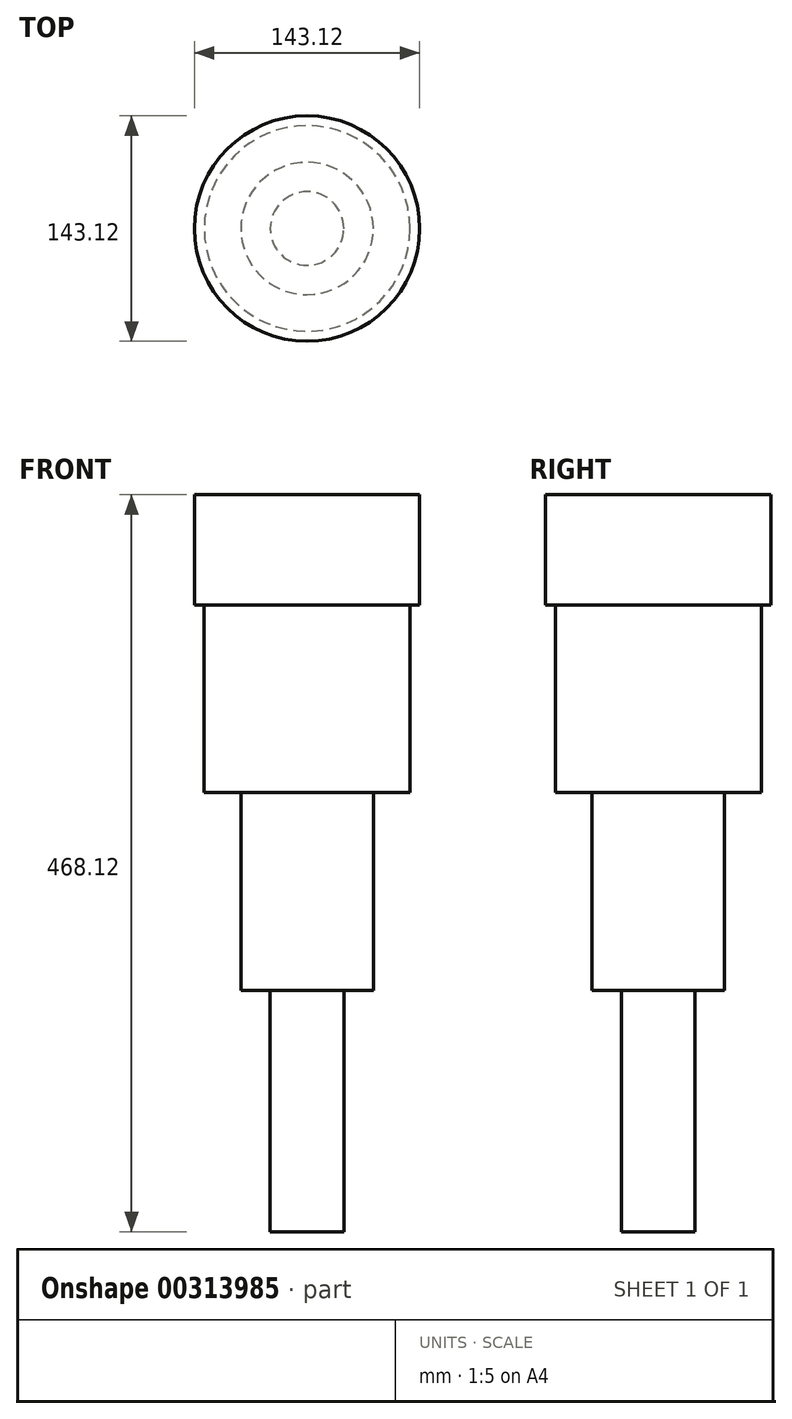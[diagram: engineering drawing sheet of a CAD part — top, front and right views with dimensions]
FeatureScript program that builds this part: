
annotation { "Feature Type Name" : "Feature", "Feature Type Description" : "" }
export const myFeature = defineFeature(function(context is Context, id is Id, definition is map)
    precondition{}
    {
        {
            var Q0;
            Q0=qCreatedBy(makeId("Top.planeOp"),FACE);
            var sketch = newSketch(context, id + "F0", { "sketchPlane" : qUnion([Q0])});
            skCircle(sketch, "E0", {"center": v(0, 0) * mm, "radius": 71.56 * mm});
            skSolve(sketch);
        }
        {
            var Q0;
            Q0 = qSketchRegion(id + "F0", true);
            extrude(context, id + "F1", {"entities" : qUnion([Q0]), "depth" : 70.1 * mm});
        }
        {
            var Q0;
            Q0=qCreatedBy(makeId("Top.planeOp"),FACE);
            var sketch = newSketch(context, id + "F2", { "sketchPlane" : qUnion([Q0])});
            skCircle(sketch, "E1", {"center": v(0, 0) * mm, "radius": 65.31 * mm});
            skSolve(sketch);
        }
        {
            var Q0;
            Q0 = qSketchRegion(id + "F2", true);
            extrude(context, id + "F3", {"entities" : qUnion([Q0]), "operationType" : NewBodyOperationType.ADD, "depth" : 62.23 * mm, "hasSecondDirection" : true, "secondDirectionOppositeDirection" : true, "secondDirectionDepth" : 119.13 * mm});
        }
        {
            var Q0;
            Q0=qCreatedBy(makeId("Top.planeOp"),FACE);
            var sketch = newSketch(context, id + "F4", { "sketchPlane" : qUnion([Q0])});
            skCircle(sketch, "E2", {"center": v(0, 0) * mm, "radius": 42.05 * mm});
            skSolve(sketch);
        }
        {
            var Q0;
            Q0 = qSketchRegion(id + "F4", true);
            extrude(context, id + "F5", {"entities" : qUnion([Q0]), "operationType" : NewBodyOperationType.ADD, "depth" : 25.4 * mm, "hasSecondDirection" : true, "secondDirectionOppositeDirection" : true, "secondDirectionDepth" : 244.86 * mm});
        }
        {
            var Q0;
            Q0=qCreatedBy(makeId("Top.planeOp"),FACE);
            var sketch = newSketch(context, id + "F6", { "sketchPlane" : qUnion([Q0])});
            skCircle(sketch, "E3", {"center": v(0, 0) * mm, "radius": 23.37 * mm});
            skSolve(sketch);
        }
        {
            var Q0;
            Q0 = qSketchRegion(id + "F6", true);
            extrude(context, id + "F7", {"entities" : qUnion([Q0]), "operationType" : NewBodyOperationType.ADD, "depth" : 25.4 * mm, "hasSecondDirection" : true, "secondDirectionOppositeDirection" : true, "secondDirectionDepth" : 398.02 * mm});
        }
    });
